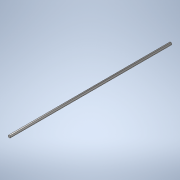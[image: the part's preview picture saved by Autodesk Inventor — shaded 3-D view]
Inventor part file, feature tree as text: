
AUTODESK INVENTOR PART (.ipt)
format: ipt  version: 2020 (Build 240168000, 168)  size: 110,592 bytes
history: native  units: in
note: dims shown in document units (in); Inventor stores cm internally (conversion verified against a paired STEP export)
features: extrude x1, sketch x1
ambient origin geometry x8: Origin, YZ Plane, XZ Plane, XY Plane, X Axis, Y Axis, Z Axis, Center Point
bodies: Solid1 (feature_tree)
feature tree (2):
  extrude  "Extrusion1"  Depth=37.0in TaperAngle=0.0deg
  sketch  "Sketch1"  dims[d0=0.5in d1=37.0in d2=0.0in]
